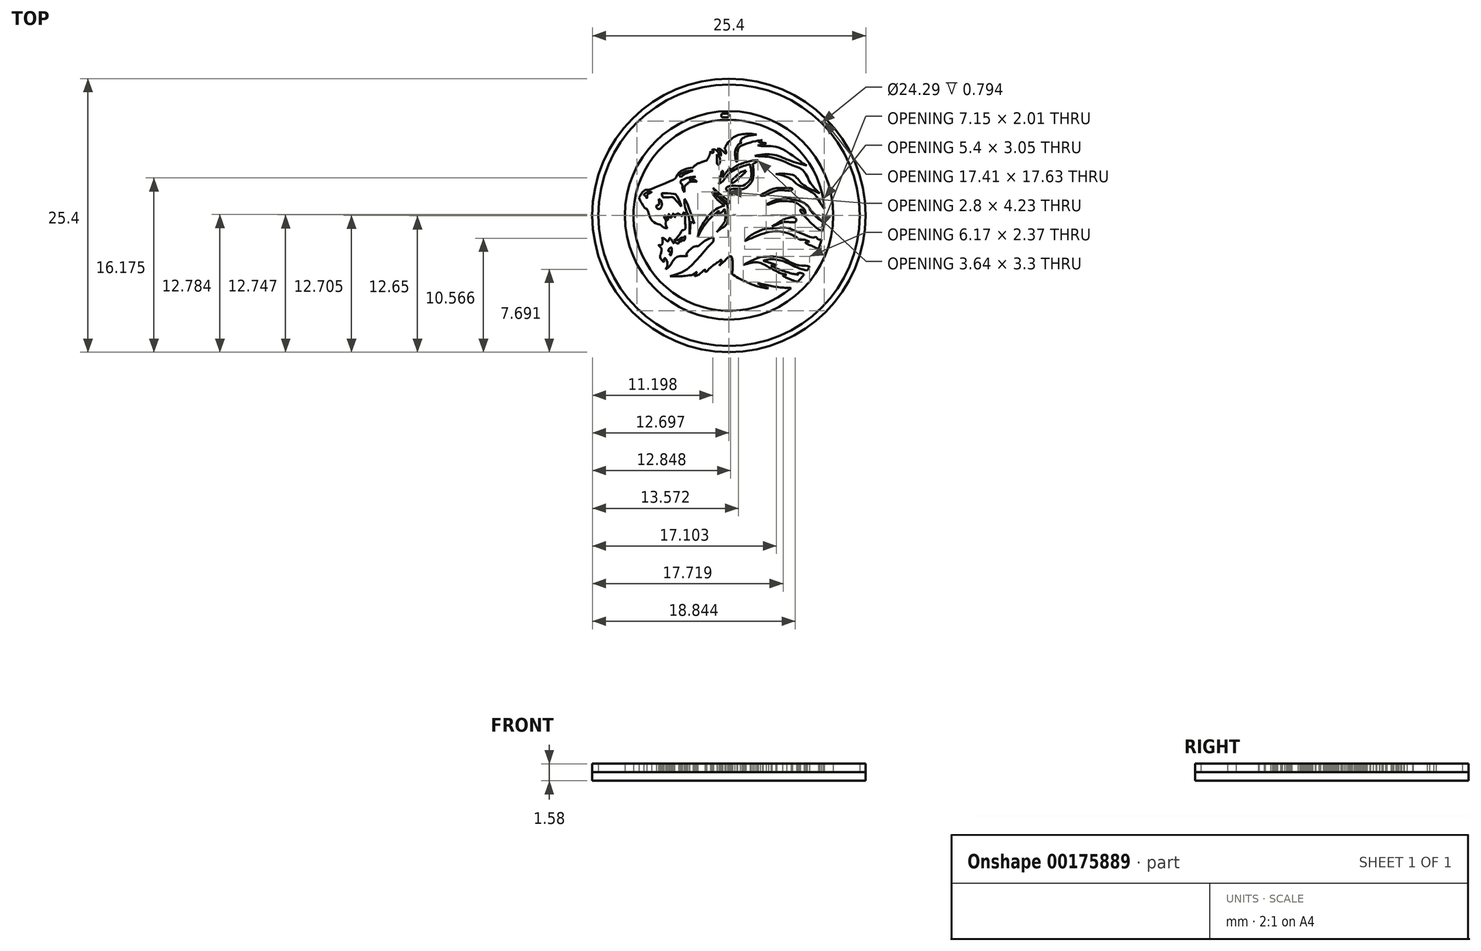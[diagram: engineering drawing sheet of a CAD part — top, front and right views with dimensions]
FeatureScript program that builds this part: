
annotation { "Feature Type Name" : "Feature", "Feature Type Description" : "" }
export const myFeature = defineFeature(function(context is Context, id is Id, definition is map)
    precondition{}
    {
        {
            var Q0;
            Q0=qCreatedBy(makeId("Top.planeOp"),FACE);
            var sketch = newSketch(context, id + "F0", { "sketchPlane" : qUnion([Q0])});
            skFitSpline(sketch, "E0", {"points": [v(12.28, 16.03) * mm, v(12.46, 15.65) * mm, v(12.9, 15.17) * mm, v(13.44, 14.76) * mm], "startDerivative": vector(0.34, -1.62) * mm, "endDerivative": vector(1.55, -1.06) * mm});
            skFitSpline(sketch, "E1", {"points": [v(13.44, 14.76) * mm, v(12.97, 14.59) * mm, v(12.27, 14.13) * mm, v(11.73, 13.52) * mm, v(11.12, 12.5) * mm, v(10.95, 11.8) * mm], "startDerivative": vector(-2.84, -0.85) * mm, "endDerivative": vector(-0.58, -3.46) * mm});
            skFitSpline(sketch, "E2", {"points": [v(10.95, 11.8) * mm, v(11.27, 12.45) * mm, v(12.01, 13.47) * mm, v(12.91, 14.26) * mm], "startDerivative": vector(1, 2.22) * mm, "endDerivative": vector(2.6, 2.04) * mm});
            skFitSpline(sketch, "E3", {"points": [v(12.91, 14.26) * mm, v(12.78, 14) * mm, v(12.7, 13.88) * mm], "startDerivative": vector(-0.25, -0.48) * mm, "endDerivative": vector(-0.15, -0.37) * mm});
            skFitSpline(sketch, "E4", {"points": [v(12.7, 13.88) * mm, v(13.1, 14.08) * mm, v(13.44, 14.42) * mm], "startDerivative": vector(0.73, 0.48) * mm, "endDerivative": vector(0.64, 0.7) * mm});
            skFitSpline(sketch, "E5", {"points": [v(13.44, 14.42) * mm, v(13.5, 13.88) * mm, v(13.48, 13.3) * mm], "startDerivative": vector(0.16, -1.17) * mm, "endDerivative": vector(-0.1, -1.08) * mm});
            skFitSpline(sketch, "E6", {"points": [v(13.48, 13.3) * mm, v(13.1, 12.79) * mm, v(12.7, 12.29) * mm], "startDerivative": vector(-0.75, -1.04) * mm, "endDerivative": vector(-0.8, -1) * mm});
            skFitSpline(sketch, "E7", {"points": [v(12.7, 12.29) * mm, v(13.13, 12.6) * mm, v(13.62, 13.01) * mm, v(13.75, 13.7) * mm, v(13.7, 14.83) * mm], "startDerivative": vector(1.89, 1.48) * mm, "endDerivative": vector(-0.24, 3.8) * mm});
            skFitSpline(sketch, "E8", {"points": [v(12.28, 16.03) * mm, v(12.72, 15.65) * mm, v(13.21, 15.19) * mm, v(13.7, 14.83) * mm], "startDerivative": vector(1.48, -1) * mm, "endDerivative": vector(1.53, -0.98) * mm});
            skFitSpline(sketch, "E9", {"points": [v(13.87, 14.97) * mm, v(13.62, 15.07) * mm, v(12.74, 15.87) * mm, v(12.36, 16.4) * mm], "startDerivative": vector(-1, 0.2) * mm, "endDerivative": vector(-0.87, 1.43) * mm});
            skFitSpline(sketch, "E10", {"points": [v(13.87, 14.97) * mm, v(13.92, 15.09) * mm, v(13.75, 15.25) * mm, v(13.04, 15.79) * mm, v(12.36, 16.4) * mm], "startDerivative": vector(0.59, 0.91) * mm, "endDerivative": vector(-1.83, 1.72) * mm});
            skFitSpline(sketch, "E11", {"points": [v(5.48, 15.48) * mm, v(5.72, 15.85) * mm, v(5.93, 16.1) * mm, v(6.06, 16.2) * mm, v(6.22, 16.2) * mm, v(6.73, 16.32) * mm, v(8.57, 17.1) * mm, v(8.89, 17.31) * mm, v(9.1, 17.72) * mm, v(9.6, 18.04) * mm, v(10.03, 18.2) * mm, v(10.49, 18.28) * mm], "startDerivative": vector(2.7, 4.46) * mm, "endDerivative": vector(5.17, 0.75) * mm});
            skFitSpline(sketch, "E12", {"points": [v(5.48, 15.48) * mm, v(5.71, 14.97) * mm, v(6.1, 14.47) * mm, v(6.2, 14.44) * mm, v(6.46, 13.78) * mm, v(6.84, 13.2) * mm, v(7.27, 13.02) * mm, v(7.47, 12.96) * mm, v(7.7, 12.76) * mm, v(8.11, 12.62) * mm], "startDerivative": vector(1.5, -3.68) * mm, "endDerivative": vector(4.11, -0.87) * mm});
            skCircle(sketch, "E13", {"center": v(13.85, 13.83) * mm, "radius": 12.7 * mm});
            skPoint(sketch, "E13.first.point", {"position": v(3.88, 5.96) * mm});
            skPoint(sketch, "E13.second.point", {"position": v(23.89, 21.61) * mm});
            skPoint(sketch, "E13.third.point", {"position": v(19.46, 2.44) * mm});
            skFitSpline(sketch, "E14", {"points": [v(10.49, 18.28) * mm, v(10.76, 18.53) * mm, v(11.31, 18.79) * mm, v(11.77, 18.93) * mm], "startDerivative": vector(0.8, 0.88) * mm, "endDerivative": vector(1.32, 0.36) * mm});
            skFitSpline(sketch, "E15", {"points": [v(11.77, 18.93) * mm, v(11.98, 19.3) * mm, v(12.08, 19.54) * mm, v(12.12, 19.79) * mm], "startDerivative": vector(0.57, 1) * mm, "endDerivative": vector(0.1, 0.84) * mm});
            skFitSpline(sketch, "E16", {"points": [v(12.12, 19.79) * mm, v(12.3, 19.63) * mm, v(12.4, 19.7) * mm, v(12.41, 19.79) * mm, v(12.36, 19.86) * mm, v(12.26, 19.9) * mm], "startDerivative": vector(0.67, -0.94) * mm, "endDerivative": vector(-0.63, 0.2) * mm});
            skFitSpline(sketch, "E17", {"points": [v(12.26, 19.9) * mm, v(12.35, 19.95) * mm, v(12.58, 19.93) * mm, v(12.67, 19.89) * mm, v(12.78, 19.76) * mm, v(12.87, 19.64) * mm, v(13.08, 19.35) * mm], "startDerivative": vector(0.54, 0.46) * mm, "endDerivative": vector(0.79, -1.45) * mm});
            skFitSpline(sketch, "E18", {"points": [v(13.08, 19.35) * mm, v(13.1, 19.57) * mm, v(13.08, 19.66) * mm, v(13.02, 19.76) * mm, v(12.94, 19.83) * mm, v(12.74, 20) * mm], "startDerivative": vector(0.23, 1.1) * mm, "endDerivative": vector(-0.6, 0.58) * mm});
            skFitSpline(sketch, "E19", {"points": [v(12.74, 20) * mm, v(12.96, 20) * mm, v(13.17, 19.89) * mm, v(13.38, 19.7) * mm, v(13.5, 19.6) * mm, v(13.55, 19.58) * mm, v(13.57, 19.7) * mm, v(13.56, 19.79) * mm, v(13.54, 19.85) * mm, v(13.5, 19.97) * mm, v(13.46, 20.03) * mm, v(13.45, 20.05) * mm], "startDerivative": vector(1.78, 0.2) * mm, "endDerivative": vector(-0.32, 0.4) * mm});
            skFitSpline(sketch, "E20", {"points": [v(13.45, 20.05) * mm, v(13.63, 20.42) * mm, v(14.24, 21.07) * mm, v(14.8, 21.32) * mm, v(15.58, 21.41) * mm, v(16.4, 21.35) * mm], "startDerivative": vector(0.82, 2.24) * mm, "endDerivative": vector(3.75, -0.48) * mm});
            skFitSpline(sketch, "E21", {"points": [v(16.4, 21.35) * mm, v(15.65, 21.22) * mm, v(15.1, 21) * mm, v(14.93, 20.79) * mm, v(14.92, 20.62) * mm, v(15.03, 20.57) * mm], "startDerivative": vector(-2.56, -0.32) * mm, "endDerivative": vector(1.15, -0.29) * mm});
            skFitSpline(sketch, "E22", {"points": [v(15.03, 20.57) * mm, v(14.8, 20.49) * mm, v(14.44, 19.9) * mm, v(14.42, 19.4) * mm, v(14.44, 19.15) * mm, v(14.46, 19.04) * mm, v(14.5, 18.9) * mm, v(14.56, 18.82) * mm], "startDerivative": vector(-1.58, -0.13) * mm, "endDerivative": vector(1.64, -0.35) * mm});
            skFitSpline(sketch, "E23", {"points": [v(14.56, 18.82) * mm, v(14.64, 18.9) * mm, v(14.62, 19.22) * mm, v(14.63, 19.6) * mm, v(14.73, 20.06) * mm, v(15.02, 20.32) * mm, v(16.43, 20.75) * mm, v(16.94, 20.81) * mm], "startDerivative": vector(1.5, 0.7) * mm, "endDerivative": vector(2.7, 0.49) * mm});
            skFitSpline(sketch, "E24", {"points": [v(16.94, 20.81) * mm, v(16.6, 20.69) * mm, v(16.62, 20.62) * mm, v(16.79, 20.61) * mm, v(17.33, 20.52) * mm], "startDerivative": vector(-1.6, -0.37) * mm, "endDerivative": vector(1.66, -0.17) * mm});
            skFitSpline(sketch, "E25", {"points": [v(17.33, 20.52) * mm, v(16.94, 20.43) * mm, v(16.51, 20.32) * mm], "startDerivative": vector(-0.8, -0.17) * mm, "endDerivative": vector(-0.84, -0.23) * mm});
            skFitSpline(sketch, "E26", {"points": [v(16.51, 20.32) * mm, v(16.83, 20.27) * mm, v(16.94, 20.26) * mm, v(17.45, 20.28) * mm, v(18.02, 20.24) * mm, v(18.76, 20) * mm, v(19.38, 19.63) * mm, v(20.24, 19.04) * mm, v(20.67, 18.7) * mm, v(21.08, 18.46) * mm], "startDerivative": vector(4.25, -0.79) * mm, "endDerivative": vector(5.36, -2.86) * mm});
            skFitSpline(sketch, "E27", {"points": [v(21.08, 18.46) * mm, v(20.34, 18.65) * mm, v(19.16, 19.06) * mm, v(18.37, 19.37) * mm, v(17.38, 19.51) * mm, v(16.25, 19.36) * mm], "startDerivative": vector(-3.8, 1.12) * mm, "endDerivative": vector(-5.3, -1.01) * mm});
            skFitSpline(sketch, "E28", {"points": [v(16.25, 19.36) * mm, v(16.83, 19.3) * mm, v(17.31, 19.29) * mm, v(17.86, 19.2) * mm, v(18.5, 19.01) * mm, v(19.09, 18.79) * mm, v(19.8, 18.46) * mm, v(20.54, 18.18) * mm, v(21.12, 17.44) * mm, v(21.33, 16.95) * mm, v(21.6, 16.58) * mm, v(21.67, 16.5) * mm, v(21.9, 16.23) * mm, v(22.3, 15.89) * mm], "startDerivative": vector(5.75, -0.47) * mm, "endDerivative": vector(5.14, -4.14) * mm});
            skFitSpline(sketch, "E29", {"points": [v(10.89, 16.95) * mm, v(10.2, 16.95) * mm, v(10.02, 16.8) * mm, v(9.79, 16.61) * mm, v(9.7, 15.98) * mm], "startDerivative": vector(-2.7, 0.24) * mm, "endDerivative": vector(0.36, -4.65) * mm});
            skFitSpline(sketch, "E30", {"points": [v(10.89, 16.95) * mm, v(10.62, 17.14) * mm, v(10.46, 17.14) * mm, v(10.2, 17.13) * mm, v(10.27, 17.24) * mm, v(10.38, 17.32) * mm, v(10.58, 17.37) * mm, v(10.63, 17.39) * mm, v(10.75, 17.42) * mm], "startDerivative": vector(-1.69, 1.43) * mm, "endDerivative": vector(1.9, 0.44) * mm});
            skFitSpline(sketch, "E31", {"points": [v(9.7, 15.98) * mm, v(9.55, 16.24) * mm, v(9.51, 16.67) * mm], "startDerivative": vector(-0.58, 0.7) * mm, "endDerivative": vector(0.17, 1.03) * mm});
            skFitSpline(sketch, "E32", {"points": [v(9.51, 16.67) * mm, v(9.39, 16.82) * mm, v(9.35, 17) * mm, v(9.51, 17.13) * mm, v(9.73, 17.22) * mm, v(10.04, 17.33) * mm, v(10.75, 17.42) * mm], "startDerivative": vector(-1.1, 0.9) * mm, "endDerivative": vector(2.82, 0.05) * mm});
            skFitSpline(sketch, "E33", {"points": [v(6.67, 15.97) * mm, v(6.45, 15.88) * mm, v(6.3, 15.77) * mm, v(6.25, 15.66) * mm, v(6.24, 15.6) * mm, v(6.23, 15.5) * mm, v(6.23, 15.37) * mm], "startDerivative": vector(-1, -0.12) * mm, "endDerivative": vector(0.03, -0.3) * mm});
            skFitSpline(sketch, "E34", {"points": [v(6.23, 15.37) * mm, v(6.12, 15.57) * mm, v(5.92, 15.76) * mm], "startDerivative": vector(-0.2, 0.44) * mm, "endDerivative": vector(-0.42, 0.34) * mm});
            skFitSpline(sketch, "E35", {"points": [v(5.92, 15.76) * mm, v(6.07, 15.88) * mm, v(6.3, 16) * mm, v(6.55, 16.02) * mm, v(6.67, 15.97) * mm], "startDerivative": vector(0.6, 0.49) * mm, "endDerivative": vector(0.46, -0.56) * mm});
            skFitSpline(sketch, "E36", {"points": [v(9.42, 14.67) * mm, v(9.17, 14.95) * mm, v(8.78, 15.38) * mm, v(8.63, 15.5) * mm, v(8.23, 15.51) * mm, v(7.83, 15.5) * mm, v(7.7, 15.51) * mm, v(7.67, 15.58) * mm, v(7.64, 15.64) * mm, v(7.6, 15.75) * mm, v(7.6, 15.86) * mm, v(8.14, 15.88) * mm, v(8.8, 15.82) * mm, v(9, 15.64) * mm, v(9.42, 14.67) * mm]});
            skFitSpline(sketch, "E37", {"points": [v(7.34, 15.35) * mm, v(7.35, 14.83) * mm, v(7.16, 14.78) * mm, v(7.1, 14.63) * mm, v(7.19, 14.45) * mm, v(7.3, 14.43) * mm, v(7.38, 14.43) * mm, v(7.46, 14.47) * mm, v(7.6, 14.76) * mm, v(7.57, 15.08) * mm, v(7.34, 15.35) * mm]});
            skFitSpline(sketch, "E38", {"points": [v(8.11, 12.62) * mm, v(7.99, 12.84) * mm, v(7.96, 13.07) * mm, v(7.98, 13.3) * mm, v(7.9, 13.56) * mm, v(7.8, 13.7) * mm, v(7.8, 13.73) * mm, v(7.86, 13.83) * mm, v(7.95, 13.8) * mm, v(8, 13.7) * mm, v(8.15, 13.41) * mm, v(8.24, 13.9) * mm, v(8.27, 13.96) * mm, v(8.33, 13.93) * mm, v(8.37, 13.72) * mm, v(8.42, 13.57) * mm, v(8.46, 13.59) * mm, v(8.62, 13.93) * mm, v(8.64, 14) * mm, v(8.74, 13.95) * mm, v(8.77, 13.76) * mm, v(8.8, 13.65) * mm, v(8.87, 13.71) * mm, v(8.94, 13.96) * mm, v(9.29, 13.98) * mm, v(9.36, 13.8) * mm, v(9.5, 13.77) * mm, v(9.57, 13.98) * mm, v(9.67, 14.15) * mm], "startDerivative": vector(-3.52, 4.82) * mm, "endDerivative": vector(3.28, 3.73) * mm});
            skFitSpline(sketch, "E39", {"points": [v(9.67, 14.15) * mm, v(9.76, 13.93) * mm, v(9.78, 13.66) * mm, v(9.78, 13.19) * mm, v(9.8, 12.84) * mm, v(9.8, 12.78) * mm, v(9.8, 12.62) * mm, v(9.63, 12.46) * mm, v(9.52, 12.44) * mm, v(9.25, 12.06) * mm, v(8.6, 11.4) * mm], "startDerivative": vector(1.08, -2.41) * mm, "endDerivative": vector(-4.17, -3.08) * mm});
            skFitSpline(sketch, "E40", {"points": [v(8.6, 11.4) * mm, v(8.33, 11.73) * mm, v(8.18, 11.41) * mm, v(8, 11.53) * mm, v(7.65, 11.78) * mm], "startDerivative": vector(-1.25, 1.64) * mm, "endDerivative": vector(-1.32, 0.8) * mm});
            skFitSpline(sketch, "E41", {"points": [v(7.65, 11.78) * mm, v(7.59, 11.1) * mm, v(7.3, 11.06) * mm, v(7.57, 10.73) * mm, v(7.45, 10.13) * mm, v(7.44, 9.97) * mm, v(7.52, 9.8) * mm, v(7.79, 9.47) * mm], "startDerivative": vector(0.66, -4.7) * mm, "endDerivative": vector(2, -2.32) * mm});
            skFitSpline(sketch, "E42", {"points": [v(7.79, 9.47) * mm, v(7.87, 9.87) * mm, v(8.06, 9.63) * mm, v(8.11, 9.17) * mm, v(7.97, 8.8) * mm], "startDerivative": vector(0.11, 2.29) * mm, "endDerivative": vector(-0.7, -1.41) * mm});
            skFitSpline(sketch, "E43", {"points": [v(7.97, 8.8) * mm, v(8.28, 9.07) * mm, v(8.51, 9.4) * mm, v(8.71, 9.71) * mm, v(9.04, 9.98) * mm, v(9.55, 10.04) * mm, v(9.99, 10.07) * mm], "startDerivative": vector(2, 1.5) * mm, "endDerivative": vector(2.5, 0.2) * mm});
            skFitSpline(sketch, "E44", {"points": [v(9.99, 10.07) * mm, v(9.87, 10.23) * mm, v(10.66, 10.96) * mm, v(10.86, 10.96) * mm, v(11.04, 11) * mm, v(11.13, 11.08) * mm, v(11.58, 11.45) * mm, v(12.1, 11.72) * mm, v(12.38, 11.78) * mm, v(12.4, 11.57) * mm, v(12.38, 11.4) * mm, v(12.04, 11.04) * mm, v(11.18, 10.07) * mm, v(9.86, 8.77) * mm, v(8.36, 8.16) * mm], "startDerivative": vector(-4.67, 2.54) * mm, "endDerivative": vector(-12.33, -3.45) * mm});
            skFitSpline(sketch, "E45", {"points": [v(8.36, 8.16) * mm, v(9.27, 8.16) * mm, v(9.34, 8.16) * mm, v(10.34, 8.28) * mm, v(10.44, 8.3) * mm, v(10.9, 8.6) * mm], "startDerivative": vector(4.4, 0.02) * mm, "endDerivative": vector(3.17, 2.29) * mm});
            skFitSpline(sketch, "E46", {"points": [v(10.9, 8.6) * mm, v(10.8, 8.44) * mm, v(10.65, 8.19) * mm], "startDerivative": vector(-0.2, -0.34) * mm, "endDerivative": vector(-0.28, -0.49) * mm});
            skFitSpline(sketch, "E47", {"points": [v(10.65, 8.19) * mm, v(11.18, 8.43) * mm, v(11.62, 8.8) * mm, v(11.62, 8.66) * mm, v(11.72, 8.55) * mm], "startDerivative": vector(1.48, 0.42) * mm, "endDerivative": vector(0.6, -0.54) * mm});
            skFitSpline(sketch, "E48", {"points": [v(11.72, 8.55) * mm, v(12.4, 9.2) * mm, v(12.94, 9.58) * mm, v(13.1, 9.7) * mm, v(13.18, 9.62) * mm, v(12.95, 9.17) * mm], "startDerivative": vector(2.21, 2.4) * mm, "endDerivative": vector(-1.7, -2.43) * mm});
            skFitSpline(sketch, "E49", {"points": [v(12.95, 9.17) * mm, v(13.47, 9.65) * mm, v(13.76, 9.93) * mm, v(14.05, 10.03) * mm, v(14.15, 9.73) * mm, v(14.17, 9.47) * mm, v(14.17, 9.27) * mm, v(14.17, 9.1) * mm, v(14.17, 9) * mm, v(14.17, 8.88) * mm, v(14.17, 8.73) * mm, v(14.14, 8.55) * mm, v(14.11, 8.47) * mm, v(14.12, 8.4) * mm], "startDerivative": vector(3.77, 3.56) * mm, "endDerivative": vector(0.34, -1.57) * mm});
            skFitSpline(sketch, "E50", {"points": [v(17.52, 7.08) * mm, v(17.47, 7.05) * mm, v(17.01, 7.11) * mm, v(16.47, 7.24) * mm, v(16, 7.4) * mm, v(14.83, 7.95) * mm, v(14.12, 8.4) * mm], "startDerivative": vector(-0.72, -0.03) * mm, "endDerivative": vector(-3.1, 2.02) * mm});
            skFitSpline(sketch, "E51", {"points": [v(17.52, 7.08) * mm, v(17.1, 7.24) * mm, v(17, 7.27) * mm, v(16.49, 7.55) * mm], "startDerivative": vector(-1.42, 0.52) * mm, "endDerivative": vector(-1.45, 0.83) * mm});
            skFitSpline(sketch, "E52", {"points": [v(16.49, 7.55) * mm, v(17.2, 7.39) * mm, v(18.44, 7.16) * mm, v(19.6, 7.08) * mm], "startDerivative": vector(2.3, -0.55) * mm, "endDerivative": vector(3.02, -0.16) * mm});
            skCircle(sketch, "E53.0", {"center": v(13.85, 13.83) * mm, "radius": 12.15 * mm});
            skCircle(sketch, "E54.0", {"center": v(13.85, 13.83) * mm, "radius": 9.68 * mm});
            skCircle(sketch, "E55.0", {"center": v(13.85, 13.83) * mm, "radius": 8.88 * mm});
            skFitSpline(sketch, "E56", {"points": [v(22.3, 15.89) * mm, v(21.33, 16.3) * mm, v(20.6, 16.8) * mm, v(20.21, 17.23) * mm, v(19.74, 17.6) * mm, v(18.17, 17.68) * mm], "startDerivative": vector(-4.6, 1.8) * mm, "endDerivative": vector(-6.89, -0.26) * mm});
            skFitSpline(sketch, "E57", {"points": [v(18.17, 17.68) * mm, v(18.74, 17.56) * mm, v(19.55, 17.26) * mm, v(20.02, 16.85) * mm, v(20.45, 16.56) * mm, v(20.9, 16.32) * mm, v(21.77, 15.8) * mm, v(22.36, 14.94) * mm, v(22.7, 14.48) * mm], "startDerivative": vector(4.61, -0.96) * mm, "endDerivative": vector(2.75, -3.53) * mm});
            skFitSpline(sketch, "E58", {"points": [v(19.68, 16.14) * mm, v(18.91, 16.15) * mm, v(18.27, 16.12) * mm, v(17.81, 15.96) * mm, v(17.37, 15.78) * mm, v(17.03, 15.65) * mm, v(16.76, 15.7) * mm, v(17.11, 15.91) * mm, v(17.53, 16.1) * mm, v(18.03, 16.32) * mm, v(18.66, 16.36) * mm, v(19.5, 16.38) * mm, v(19.72, 16.31) * mm, v(19.68, 16.14) * mm]});
            skFitSpline(sketch, "E59", {"points": [v(22.7, 13.11) * mm, v(22.32, 13.36) * mm, v(21.68, 13.96) * mm, v(21.35, 14.42) * mm, v(21.08, 14.82) * mm, v(20.3, 15.18) * mm, v(19.47, 15.38) * mm, v(18.46, 15.34) * mm, v(17.3, 14.83) * mm], "startDerivative": vector(-3.6, 2.2) * mm, "endDerivative": vector(-7.3, -3.83) * mm});
            skFitSpline(sketch, "E60", {"points": [v(22.6, 12.35) * mm, v(22.1, 12.57) * mm, v(21.28, 13.31) * mm, v(20.53, 14.15) * mm, v(20.47, 14.32) * mm, v(20.55, 14.38) * mm, v(20.94, 13.99) * mm], "startDerivative": vector(-2.9, 0.96) * mm, "endDerivative": vector(2.61, -3.4) * mm});
            skFitSpline(sketch, "E61", {"points": [v(20.94, 13.99) * mm, v(20.88, 14.32) * mm, v(20.42, 14.79) * mm, v(19.77, 15.1) * mm, v(18.91, 15.15) * mm, v(18.27, 15.1) * mm, v(17.61, 14.86) * mm, v(17.3, 14.83) * mm], "startDerivative": vector(-0.1, 3.05) * mm, "endDerivative": vector(-2.76, 0.09) * mm});
            skFitSpline(sketch, "E62", {"points": [v(20.11, 13.43) * mm, v(19.89, 13.64) * mm, v(19.03, 13.5) * mm, v(18.4, 13.16) * mm, v(17.83, 12.8) * mm], "startDerivative": vector(-0.9, 1.55) * mm, "endDerivative": vector(-2.2, -1.44) * mm});
            skFitSpline(sketch, "E63", {"points": [v(20.11, 13.43) * mm, v(19.97, 13.22) * mm, v(19.47, 13.2) * mm, v(19, 13.22) * mm, v(18.28, 12.96) * mm, v(17.83, 12.8) * mm], "startDerivative": vector(-0.68, -1.66) * mm, "endDerivative": vector(-2.07, -0.68) * mm});
            skFitSpline(sketch, "E64", {"points": [v(22.15, 10.7) * mm, v(21.62, 10.95) * mm, v(21.07, 11.19) * mm, v(20.94, 11.29) * mm, v(21.08, 11.36) * mm, v(21.34, 11.4) * mm], "startDerivative": vector(-1.88, 0.99) * mm, "endDerivative": vector(1.42, 0.17) * mm});
            skFitSpline(sketch, "E65", {"points": [v(21.34, 11.4) * mm, v(20.84, 11.58) * mm, v(20.39, 11.58) * mm], "startDerivative": vector(-0.98, 0.16) * mm, "endDerivative": vector(-1.07, 0.18) * mm});
            skFitSpline(sketch, "E66", {"points": [v(21.34, 9.07) * mm, v(20.88, 9.18) * mm, v(20.4, 9.18) * mm, v(19.28, 9.61) * mm, v(18.66, 9.93) * mm, v(17.56, 10) * mm, v(16.55, 9.88) * mm, v(15.11, 9.2) * mm], "startDerivative": vector(-4.53, 1.43) * mm, "endDerivative": vector(-7.92, -4.35) * mm});
            skFitSpline(sketch, "E67", {"points": [v(15.17, 9.23) * mm, v(16.12, 9.46) * mm, v(16.84, 9.38) * mm, v(18.25, 8.63) * mm, v(19.19, 8.31) * mm], "startDerivative": vector(4.15, 1.17) * mm, "endDerivative": vector(3.6, -0.88) * mm});
            skFitSpline(sketch, "E68", {"points": [v(19.19, 8.31) * mm, v(18.84, 8.26) * mm, v(20.2, 7.63) * mm], "startDerivative": vector(-1.57, -0.05) * mm, "endDerivative": vector(3.05, -1.17) * mm});
            skFitSpline(sketch, "E69", {"points": [v(21.09, 8.7) * mm, v(20.2, 8.97) * mm, v(19.08, 9.49) * mm, v(18.4, 9.7) * mm, v(17.62, 9.75) * mm, v(17.02, 9.61) * mm], "startDerivative": vector(-4.01, 1.03) * mm, "endDerivative": vector(-3.35, -1) * mm});
            skFitSpline(sketch, "E70", {"points": [v(17.02, 9.61) * mm, v(17.83, 9.37) * mm, v(18.29, 9.2) * mm], "startDerivative": vector(1.52, -0.44) * mm, "endDerivative": vector(1, -0.38) * mm});
            skFitSpline(sketch, "E71", {"points": [v(18.29, 9.2) * mm, v(17.97, 9.2) * mm, v(17.75, 9.14) * mm], "startDerivative": vector(-0.61, 0.03) * mm, "endDerivative": vector(-0.46, -0.15) * mm});
            skFitSpline(sketch, "E72", {"points": [v(17.75, 9.14) * mm, v(18.46, 8.83) * mm, v(19.72, 8.42) * mm, v(20.32, 8.31) * mm], "startDerivative": vector(2.02, -0.96) * mm, "endDerivative": vector(1.9, -0.27) * mm});
            skFitSpline(sketch, "E73", {"points": [v(20.32, 8.31) * mm, v(20.2, 8.43) * mm, v(20.5, 8.48) * mm, v(20.83, 8.35) * mm], "startDerivative": vector(-0.8, 0.47) * mm, "endDerivative": vector(0.74, -0.42) * mm});
            skFitSpline(sketch, "E74", {"points": [v(20.39, 11.58) * mm, v(19.79, 11.98) * mm, v(18.24, 12.36) * mm, v(16.54, 11.97) * mm, v(15.3, 11.44) * mm], "startDerivative": vector(-2.78, 2.16) * mm, "endDerivative": vector(-4.7, -2.07) * mm});
            skFitSpline(sketch, "E75", {"points": [v(15.3, 11.44) * mm, v(15.88, 11.97) * mm, v(17.17, 12.56) * mm, v(18.16, 12.63) * mm, v(19.39, 12.63) * mm, v(21.68, 11.75) * mm, v(21.91, 11.82) * mm, v(22.12, 11.62) * mm, v(22.44, 11.62) * mm], "startDerivative": vector(4.06, 4.23) * mm, "endDerivative": vector(4.47, 1.12) * mm});
            skFitSpline(sketch, "E76", {"points": [v(10.62, 13.06) * mm, v(9.74, 15.34) * mm, v(9.7, 15) * mm, v(9.86, 14.3) * mm, v(10.14, 13.55) * mm, v(10.2, 12.08) * mm], "startDerivative": vector(-3.58, 10.61) * mm, "endDerivative": vector(0.02, -7.84) * mm});
            skFitSpline(sketch, "E77", {"points": [v(10.62, 13.06) * mm, v(10.47, 13.18) * mm, v(10.31, 13.2) * mm, v(10.27, 13.06) * mm, v(10.2, 12.08) * mm], "startDerivative": vector(-0.68, 0.72) * mm, "endDerivative": vector(-0.19, -2.64) * mm});
            skFitSpline(sketch, "E78", {"points": [v(9.74, 11.95) * mm, v(9.65, 11.77) * mm, v(9.4, 11.76) * mm, v(9.31, 11.67) * mm, v(9.21, 11.6) * mm, v(8.97, 11.53) * mm, v(8.81, 11.5) * mm, v(8.73, 11.5) * mm], "startDerivative": vector(-0.28, -1.53) * mm, "endDerivative": vector(-1.1, 0.73) * mm});
            skFitSpline(sketch, "E79", {"points": [v(8.6, 11.4) * mm, v(8.72, 11.23) * mm, v(8.76, 11.36) * mm, v(8.88, 11.34) * mm, v(9.04, 11.21) * mm, v(9.2, 11.26) * mm, v(9.2, 11.4) * mm, v(9.31, 11.4) * mm, v(9.43, 11.4) * mm, v(9.44, 11.57) * mm, v(9.48, 11.58) * mm, v(9.64, 11.48) * mm, v(9.77, 11.68) * mm, v(9.74, 11.95) * mm], "startDerivative": vector(1.62, -3.16) * mm, "endDerivative": vector(-1.06, 2.49) * mm});
            skLineSegment(sketch, "E80.bottom", {"start": v(13.26, 22.93) * mm, "end": v(13.7, 22.93) * mm});
            skLineSegment(sketch, "E80.top", {"start": v(13.26, 23.3) * mm, "end": v(13.7, 23.3) * mm});
            skLineSegment(sketch, "E80.left", {"start": v(13.13, 23.06) * mm, "end": v(13.13, 23.17) * mm});
            skLineSegment(sketch, "E80.right", {"start": v(13.82, 23.06) * mm, "end": v(13.82, 23.17) * mm});
            skArc(sketch, "E81.filletArc", {"start": v(13.82, 23.17) * mm, "mid": v(13.78, 23.26) * mm, "end": v(13.7, 23.3) * mm});
            skPoint(sketch, "E82.visualSharp", {"position": v(13.82, 22.93) * mm});
            skArc(sketch, "E82.filletArc", {"start": v(13.7, 22.93) * mm, "mid": v(13.78, 22.97) * mm, "end": v(13.82, 23.06) * mm});
            skPoint(sketch, "E83.visualSharp", {"position": v(13.13, 22.93) * mm});
            skArc(sketch, "E83.filletArc", {"start": v(13.13, 23.06) * mm, "mid": v(13.17, 22.97) * mm, "end": v(13.26, 22.93) * mm});
            skArc(sketch, "E84.filletArc", {"start": v(13.26, 23.3) * mm, "mid": v(13.17, 23.26) * mm, "end": v(13.13, 23.17) * mm});
            skFitSpline(sketch, "E85", {"points": [v(16.54, 18.95) * mm, v(15.62, 18.83) * mm, v(14.5, 18.42) * mm, v(13.93, 17.96) * mm], "startDerivative": vector(-2.89, 0.18) * mm, "endDerivative": vector(-1.64, -1.61) * mm});
            skFitSpline(sketch, "E86", {"points": [v(13.26, 17.36) * mm, v(13.58, 17.82) * mm, v(13.92, 18.24) * mm], "startDerivative": vector(0.63, 0.93) * mm, "endDerivative": vector(0.7, 0.84) * mm});
            skFitSpline(sketch, "E87", {"points": [v(13.92, 18.24) * mm, v(13.92, 18.1) * mm, v(13.93, 17.96) * mm], "startDerivative": vector(0, -0.3) * mm, "endDerivative": vector(0.03, -0.28) * mm});
            skFitSpline(sketch, "E88", {"points": [v(13.26, 17.36) * mm, v(13.3, 17.75) * mm, v(13.17, 17.95) * mm], "startDerivative": vector(0.3, 1.27) * mm, "endDerivative": vector(-0.8, -0.44) * mm});
            skFitSpline(sketch, "E89", {"points": [v(13.17, 17.95) * mm, v(13.08, 17.46) * mm, v(13.03, 17.15) * mm, v(12.9, 16.76) * mm], "startDerivative": vector(-0.28, -1.41) * mm, "endDerivative": vector(-0.43, -1.2) * mm});
            skFitSpline(sketch, "E90", {"points": [v(12.9, 16.76) * mm, v(13.25, 17) * mm, v(13.54, 17.35) * mm, v(13.88, 17.73) * mm, v(14.44, 18.1) * mm, v(15.2, 18.42) * mm, v(15.8, 18.58) * mm], "startDerivative": vector(2.55, 1.48) * mm, "endDerivative": vector(3.36, 0.8) * mm});
            skFitSpline(sketch, "E91", {"points": [v(15.8, 18.58) * mm, v(15.91, 17.95) * mm, v(15.87, 17.28) * mm, v(15.5, 16.81) * mm, v(15, 16.55) * mm, v(14.03, 16.58) * mm, v(13.56, 16.35) * mm, v(13.62, 16.18) * mm, v(14.16, 15.66) * mm], "startDerivative": vector(0.93, -4.72) * mm, "endDerivative": vector(4.53, -4.14) * mm});
            skFitSpline(sketch, "E92", {"points": [v(14.16, 15.66) * mm, v(13.94, 16.07) * mm, v(13.84, 16.29) * mm], "startDerivative": vector(-0.42, 0.76) * mm, "endDerivative": vector(-0.2, 0.5) * mm});
            skFitSpline(sketch, "E93", {"points": [v(13.84, 16.29) * mm, v(14.16, 16.29) * mm, v(14.9, 16.29) * mm, v(15.23, 16.29) * mm, v(15.56, 16.51) * mm, v(15.91, 16.89) * mm, v(16.1, 17.36) * mm, v(16.07, 18.61) * mm], "startDerivative": vector(2.5, -0.03) * mm, "endDerivative": vector(-0.48, 6.5) * mm});
            skFitSpline(sketch, "E94", {"points": [v(16.07, 18.61) * mm, v(16.34, 18.75) * mm, v(16.54, 18.95) * mm], "startDerivative": vector(0.5, 0.32) * mm, "endDerivative": vector(0.33, 0.34) * mm});
            skFitSpline(sketch, "E95", {"points": [v(15.43, 17.98) * mm, v(14.92, 17.83) * mm, v(14.4, 17.4) * mm, v(14.06, 17.03) * mm, v(14.04, 16.86) * mm, v(14.25, 16.87) * mm, v(14.66, 17.2) * mm, v(15.19, 17.68) * mm, v(15.43, 17.98) * mm]});
            skFitSpline(sketch, "E96", {"points": [v(8.34, 10.46) * mm, v(8.23, 10.5) * mm, v(8.24, 10.67) * mm, v(8.4, 10.82) * mm, v(8.52, 10.82) * mm, v(8.5, 10.3) * mm, v(8.44, 10.13) * mm, v(8.37, 10.15) * mm, v(8.35, 10.26) * mm, v(8.42, 10.34) * mm, v(8.34, 10.46) * mm]});
            skFitSpline(sketch, "E97", {"points": [v(12.75, 19.5) * mm, v(13, 19.12) * mm, v(12.99, 18.71) * mm, v(12.95, 18.6) * mm, v(12.82, 18.54) * mm, v(12.71, 18.74) * mm, v(12.72, 19.08) * mm, v(12.75, 19.5) * mm]});
            skFitSpline(sketch, "E98", {"points": [v(9.4, 17.4) * mm, v(9.75, 17.68) * mm, v(10.5, 17.97) * mm], "startDerivative": vector(0.73, 0.7) * mm, "endDerivative": vector(1.47, 0.46) * mm});
            skFitSpline(sketch, "E99", {"points": [v(10.5, 17.97) * mm, v(10.17, 17.97) * mm, v(9.81, 17.89) * mm, v(9.5, 17.74) * mm, v(9.27, 17.62) * mm, v(9.27, 17.47) * mm, v(9.4, 17.4) * mm], "startDerivative": vector(-1.74, 0.08) * mm, "endDerivative": vector(1.16, -0.42) * mm});
            skSolve(sketch);
        }
        {
            var Q0;
            Q0=makeQuery(id+"F0.imprint","IMPRINT",FACE,{"disambiguationData":[TD([[makeQuery(id+"F0.imprint","IMPRINT",EDGE,{"derivedFrom":sQuery(id+"F0.wireOp",EDGE,"E0")}),-1.0]])]});
            var Q1;
            Q1=makeQuery(id+"F0.imprint","IMPRINT",FACE,{"disambiguationData":[TD([[makeQuery(id+"F0.imprint","IMPRINT",EDGE,{"derivedFrom":sQuery(id+"F0.wireOp",EDGE,"E80.bottom")}),-1.0]])]});
            var Q2;
            Q2=makeQuery(id+"F0.imprint","IMPRINT",FACE,{"disambiguationData":[TD([[makeQuery(id+"F0.imprint","IMPRINT",EDGE,{"derivedFrom":sQuery(id+"F0.wireOp",EDGE,"E80.bottom")}),1.0]])]});
            var Q3;
            Q3=makeQuery(id+"F0.imprint","IMPRINT",FACE,{"disambiguationData":[TD([[makeQuery(id+"F0.imprint","IMPRINT",EDGE,{"derivedFrom":sQuery(id+"F0.wireOp",EDGE,"E13")}),1.0]])]});
            var Q4;
            {var subQ0=sQuery(id+"F0.wireOp",EDGE,"E69");Q4=makeQuery(id+"F0.imprint","IMPRINT",FACE,{"disambiguationData":[TD([[makeQuery(id+"F0.imprint","IMPRINT",EDGE,{"derivedFrom":subQ0}),1.0]])]});}
            extrude(context, id + "F1", {"entities" : qUnion([Q0, Q1, Q2, Q3, Q4]), "depth" : 0.8 * mm});
        }
        {
            var Q0;
            Q0=makeQuery(id+"F0.imprint","IMPRINT",FACE,{"disambiguationData":[TD([[makeQuery(id+"F0.imprint","IMPRINT",EDGE,{"derivedFrom":sQuery(id+"F0.wireOp",EDGE,"E80.bottom")}),1.0]])]});
            extrude(context, id + "F2", {"entities" : qUnion([Q0]), "operationType" : NewBodyOperationType.REMOVE, "depth" : 0.8 * mm});
        }
        {
            var Q0;
            Q0=makeQuery(id+"F1.opExtrude","CAP_FACE",FACE,{"disambiguationData":[OSD([sQuery(id+"F0.wireOp",EDGE,"E13"),sQuery(id+"F0.wireOp",EDGE,"E53.0")])],"isStart":true});
            var sketch = newSketch(context, id + "F3", { "sketchPlane" : qUnion([Q0])});
            skCircle(sketch, "E100.0", {"center": v(13.85, -13.83) * mm, "radius": 12.7 * mm});
            skSolve(sketch);
        }
        {
            var Q0;
            Q0 = qSketchRegion(id + "F3", true);
            var Q1;
            Q1=makeQuery(id+"F3.imprint","IMPRINT",FACE,{"disambiguationData":[TD([[makeQuery(id+"F3.imprint","IMPRINT",EDGE,{"derivedFrom":sQuery(id+"F3.wireOp",EDGE,"E100.0")}),-1.0]])]});
            extrude(context, id + "F4", {"entities" : qUnion([Q0, Q1]), "depth" : 0.8 * mm});
        }
    });
